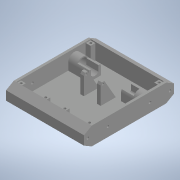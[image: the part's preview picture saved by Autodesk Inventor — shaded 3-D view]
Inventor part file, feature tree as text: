
AUTODESK INVENTOR PART (.ipt)
format: ipt  version: 2020 (Build 240168000, 168)  size: 392,704 bytes
history: native  units: in
note: dims shown in document units (in); Inventor stores cm internally (conversion verified against a paired STEP export)
features: projected_geometry x13, extrude x11, sketch x11, mirror x4, plane x1
ambient origin geometry x8: Origin, YZ Plane, XZ Plane, XY Plane, X Axis, Y Axis, Z Axis, Center Point
bodies: Solid1 (feature_tree)
feature tree (40):
  extrude  "Extrusion1"  Depth=5.9055in
  extrude  "Extrusion2"  TaperAngle=0.0deg  [1 undecoded]
  extrude  "Extrusion3"  Depth=1.063in
  extrude  "Extrusion4"  Depth=0.315in
  extrude  "Extrusion5"  TaperAngle=0.0deg  [1 undecoded]
  extrude  "Extrusion6"  Depth=0.5906in
  mirror  "Mirror1"
  extrude  "Extrusion7"  Depth=0.0787in
  mirror  "Mirror2"
  extrude  "Extrusion8"  Depth=0.5512in
  mirror  "Mirror3"
  plane  "Work Plane1"
  extrude  "Extrusion9"  Depth=0.7874in TaperAngle=0.0deg
  mirror  "Mirror4"
  extrude  "Extrusion10"  Depth=6.063in TaperAngle=0.0deg
  extrude  "Extrusion11"  Depth=0.1575in
  sketch  "Sketch1"  dims[d0=1.1811in d1=5.9055in]
  sketch  "Sketch2"  dims[d2=5.1181in d3=0.0in]
  projected_geometry  "Projected Loop1"
  sketch  "Sketch3"  dims[d4=0.1575in d5=1.063in]
  projected_geometry  "Projected Loop2"
  projected_geometry  "Projected Loop3"
  sketch  "Sketch4"  dims[d6=0.0in d8=0.315in]
  sketch  "Sketch5"  dims[d10=0.993in d11=0.0in]
  projected_geometry  "Projected Loop4"
  sketch  "Sketch6"  dims[d12=0.6496in d13=0.5906in]
  sketch  "Sketch7"  dims[d14=1.5748in d15=0.0787in]
  sketch  "Sketch9"  dims[d16=0.5512in d17=0.0in d18=0.6102in]
  sketch  "Sketch10"  dims[d19=0.4803in d20=0.7874in d21=0.0in]
  sketch  "Sketch12"  dims[d22=0.1654in d23=6.063in d24=0.0in]
  projected_geometry  "Projected Loop6"
  projected_geometry  "Projected Loop7"
  projected_geometry  "Projected Loop8"
  sketch  "Sketch13"  dims[d25=0.5114in d26=0.1575in d27=1.5748in d28=0.0in d29=0.0in d30=0.1575in d31=0.2756in d32=0.0in d33=0.4331in d34=0.122in d38=2.7559in d40=0.061in d41=0.0909in d42=0.2362in d43=0.0in d44=60.0deg d45=0.0787in d46=0.315in d48=0.993in d49=0.0in d51=0.1575in d52=0.1575in d53=0.2756in d54=0.0in d55=0.4724in]
  projected_geometry  "Projected Loop9"
  projected_geometry  "Projected Loop10"
  projected_geometry  "Projected Loop11"
  projected_geometry  "Projected Loop12"
  projected_geometry  "Projected Loop13"
  projected_geometry  "Projected Loop14"
note: 2 required parameter values undecoded (feature->parameter linkage not recoverable at this tier; creation-order binding heuristic only, values carry confidence <= 0.55)
